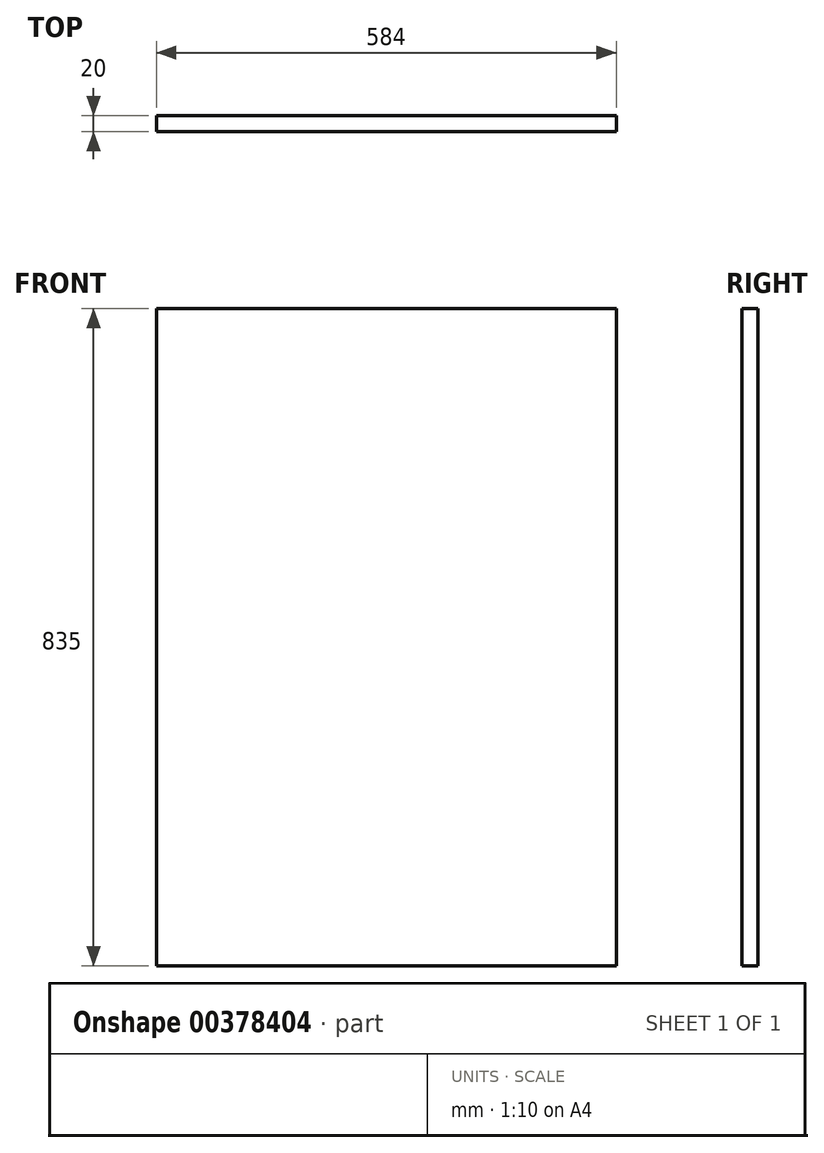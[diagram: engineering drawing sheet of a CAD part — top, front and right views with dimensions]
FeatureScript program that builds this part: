
annotation { "Feature Type Name" : "Feature", "Feature Type Description" : "" }
export const myFeature = defineFeature(function(context is Context, id is Id, definition is map)
    precondition{}
    {
        {
            var Q0;
            Q0=qCreatedBy(makeId("Front.planeOp"),FACE);
            var sketch = newSketch(context, id + "F0", { "sketchPlane" : qUnion([Q0])});
            skLineSegment(sketch, "E0.bottom", {"start": v(292, 417.5) * mm, "end": v(-292, 417.5) * mm});
            skLineSegment(sketch, "E0.top", {"start": v(292, -417.5) * mm, "end": v(-292, -417.5) * mm});
            skLineSegment(sketch, "E0.left", {"start": v(292, 417.5) * mm, "end": v(292, -417.5) * mm});
            skLineSegment(sketch, "E0.right", {"start": v(-292, 417.5) * mm, "end": v(-292, -417.5) * mm});
            skPoint(sketch, "E0.middle", {"position": v(0, 0) * mm});
            skSolve(sketch);
        }
        {
            var Q0;
            Q0 = qSketchRegion(id + "F0", true);
            extrude(context, id + "F1", {"entities" : qUnion([Q0]), "depth" : 20 * mm});
        }
    });
